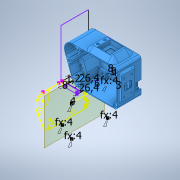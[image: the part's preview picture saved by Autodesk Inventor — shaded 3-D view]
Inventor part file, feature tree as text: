
AUTODESK INVENTOR PART (.ipt)
format: ipt  version: 2021.1 (Build 251245010, 245A)  size: 1,960,960 bytes
history: mixed  units: in
note: dims shown in document units (in); Inventor stores cm internally (conversion verified against a paired STEP export)
features: extrude x24, sketch x21, move_body x9, direct_edit x7, chamfer x6, projected_geometry x5, other x4, revolve x3, fillet x1, plane x1, imported_body x1
ambient origin geometry x8: Origin, YZ Plane, XZ Plane, XY Plane, X Axis, Y Axis, Z Axis, Center Point
bodies: Solid1 (imported_parasolid), Volumenkörper268 (imported_parasolid), Body1 (imported_parasolid)
feature tree (82):
  sketch  "Skizze1"  dims[d0=0.1575in d1=0.1575in]
  extrude  "Extrusion2"  Depth=0.1575in
  extrude  "Extrusion1"  Depth=0.1575in
  sketch  "Skizze3"  dims[d2=0.1575in d3=0.1575in]
  extrude  "Extrusion3"  Depth=0.252in TaperAngle=0.0deg
  extrude  "Extrusion4"  Depth=0.2756in TaperAngle=0.0deg
  extrude  "Extrusion5"  Depth=0.1575in
  extrude  "Extrusion6"  Depth=0.1575in
  direct_edit  "Direktbearbeitung2"
  extrude  "Extrusion8"  Depth=0.315in
  direct_edit  "Direktbearbeitung3"
  extrude  "Extrusion10"  Depth=0.1969in TaperAngle=0.0deg
  extrude  "Extrusion11"  TaperAngle=135.0deg  [1 undecoded]
  sketch  "Skizze16"  dims[d19=45.0deg d20=0.1969in d21=0.5906in d22=0.0in d23=0.0in]
  direct_edit  "Direktbearbeitung4"
  extrude  "Extrusion19"  TaperAngle=0.0deg  [1 undecoded]
  direct_edit  "Direktbearbeitung6"
  direct_edit  "Direktbearbeitung7"
  chamfer  "Fase2"  Distance=0.0157in
  extrude  "Extrusion26"  TaperAngle=135.0deg  [1 undecoded]
  chamfer  "Fase4"  Distance=0.3937in
  sketch  "Skizze29"  dims[d32=0.3937in d33=0.2362in d34=0.0in d35=0.0in d36=0.0in d37=0.0in d38=-0.0394in d39=0.0157in d40=0.0in]
  extrude  "Extrusion30"  TaperAngle=0.0deg  [1 undecoded]
  extrude  "Extrusion35"  Depth=0.3937in
  other  "Flächenverjüngung3"
  extrude  "Extrusion36"  Depth=0.315in
  revolve  "Umdrehung1"
  sketch  "Skizze36"  dims[d45=0.3937in d46=0.0in d69=0.0in d70=0.0in d71=-0.2756in]
  fillet  "Rundung3"  Radius=0.315in
  extrude  "Extrusion37"  Depth=0.1181in TaperAngle=0.0deg
  chamfer  "Fase5"  [1 undecoded]
  plane  "Arbeitsebene2"
  extrude  "Extrusion38"  Depth=0.0787in
  extrude  "Extrusion39"  Depth=0.0197in
  extrude  "Extrusion40"  Depth=0.0787in TaperAngle=45.0deg
  chamfer  "Fase6"  Distance=0.0197in
  extrude  "Extrusion41"  Depth=0.1181in
  chamfer  "Fase7"  Distance=0.0197in
  extrude  "Extrusion42"  TaperAngle=90.0deg  [1 undecoded]
  extrude  "Extrusion9"  Depth=0.0787in
  direct_edit  "Direktbearbeitung8"
  sketch  "Skizze44"  dims[d122=0.0157in d123=0.0in d124=0.0197in d125=0.0787in d126=45.0deg d133=0.0197in d134=0.0in]
  sketch  "Skizze45"  dims[d144=0.3346in d145=0.0in d147=0.1181in]
  direct_edit  "Direktbearbeitung10"
  sketch  "Skizze47"  dims[d148=45.0deg d149=0.0197in d150=0.0in]
  extrude  "Extrusion43"  Depth=0.0787in TaperAngle=0.0deg
  extrude  "Extrusion44"  Depth=0.0787in TaperAngle=45.0deg
  chamfer  "Fase8"  Distance=0.3937in
  extrude  "Extrusion45"  Depth=0.0787in
  projected_geometry  "Projizierte Kontur2"
  sketch  "Skizze4"  dims[d4=0.1575in d5=0.252in d6=0.0in]
  sketch  "Skizze5"  dims[d7=0.2362in d8=0.0in d9=0.2756in d10=0.0in]
  sketch  "Skizze8"  dims[d11=0.1575in d12=0.0in d13=0.1575in]
  sketch  "Skizze9"  dims[d14=0.1575in d15=0.1575in]
  sketch  "Skizze10"  dims[d16=0.252in d17=0.0in d18=0.315in]
  sketch  "Skizze26"  dims[d30=0.315in d31=135.0deg]
  sketch  "Skizze35"  dims[d41=0.315in d42=135.0deg d43=0.3937in d44=0.0in]
  sketch  "Skizze37"  dims[d72=0.3937in d73=0.0in d74=1.0394in]
  projected_geometry  "Projizierte Kontur7"
  sketch  "Skizze38"  dims[d75=1.0394in d76=0.0472in d86=0.315in]
  sketch  "Skizze39"  dims[d87=0.2362in d88=0.0in d89=0.0in d90=0.1181in d104=0.0in d105=0.0in d106=-0.0787in]
  projected_geometry  "Projizierte Kontur8"
  sketch  "Skizze40"  dims[d109=0.0197in d113=0.0197in d114=0.0787in d115=45.0deg d119=0.0197in]
  projected_geometry  "Projizierte Kontur9"
  sketch  "Skizze41"  dims[d120=0.0197in d121=0.0197in]
  sketch  "Skizze48"  dims[d151=0.1969in d152=90.0deg d153=0.0787in d154=0.0787in d155=0.0in d156=0.0787in d157=0.0787in d158=45.0deg d159=0.3937in d160=0.0787in d161=1.9685in d162=0.0in d163=0.1969in d164=0.1969in d165=135.0deg d166=0.0394in d167=0.0in d168=0.1575in d172=0.1811in d173=0.252in d174=0.0in d175=0.0197in d176=0.0787in d177=45.0deg d178=0.1969in d179=0.1969in d180=0.0394in d181=0.0in d182=0.0197in d183=0.0787in d184=45.0deg d185=0.0157in d186=0.0in d187=-0.6184in d188=0.0in d189=2.8346in d190=0.0in d191=4.1339in d192=0.0in d193=0.0in d194=0.0in d195=0.0in d196=1.3346in d197=-1.0433in d198=0.0in d199=0.0in d201=180.0deg d202=3.9375in d203=0.1875in d204=0.375in d205=0.1575in d206=0.315in d207=0.3937in d208=0.0in d209=0.1969in d210=0.0354in d211=0.0in d212=0.0197in d213=0.0787in d214=45.0deg d215=0.2362in d216=0.0591in d217=0.0079in d218=0.0in]
  projected_geometry  "Projizierte Kontur11"
  other  "Löschen2"
  other  "Löschen3"
  move_body  "Verschieben1"
  other  "Löschen4"
  move_body  "Verschieben2"
  move_body  "Verschieben4"
  move_body  "Verschieben5"
  revolve  "Drehen1"  [1 undecoded]
  move_body  "Verschieben6"
  move_body  "Verschieben7"
  move_body  "Verschieben8"
  move_body  "Verschieben9"
  revolve  "Drehen3"  [1 undecoded]
  move_body  "Verschieben10"
  imported_body  NMx_Import_Brep_tag  [imported B-rep: ~72 faces, bbox_mm=[106.981267, 80.0, 48.4]]
note: 8 required parameter values undecoded (feature->parameter linkage not recoverable at this tier; creation-order binding heuristic only, values carry confidence <= 0.55)